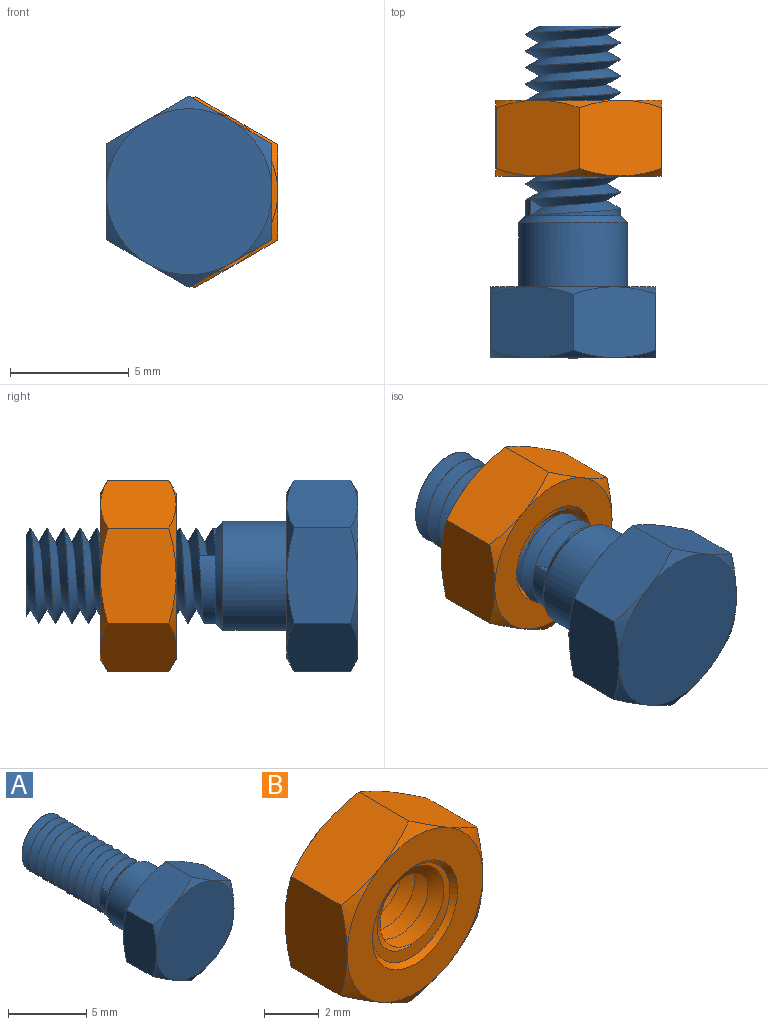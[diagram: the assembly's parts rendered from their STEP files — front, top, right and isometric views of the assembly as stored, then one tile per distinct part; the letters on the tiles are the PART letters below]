
ASSEMBLY  parts=2 mates=1
PART A: 27 faces, bbox 8.6x14.9x8.6 mm
  f0: cylinder r=2mm len=8mm, axis (0,-1,0), area 15.5mm2, adj f22,f23,f24,f25,f26
  f1: plane 7x7mm, normal (0,1,0), area 21.9mm2, adj f2,f3,f4,f5,f6,f7,f8
  f2: cylinder r=2.3mm len=4.6mm, axis (0,-1,0), area 39mm2, adj f1,f22
  f3: cone r=5.9mm half-angle=60deg, axis (0,-1,0), area 1.2mm2, adj f1,f9,f14
  f4: cone r=5.9mm half-angle=60deg, axis (0,-1,0), area 1.2mm2, adj f1,f9,f10
  f5: cone r=5.9mm half-angle=60deg, axis (0,-1,0), area 1.2mm2, adj f1,f10,f11
  f6: cone r=5.9mm half-angle=60deg, axis (0,-1,0), area 1.2mm2, adj f1,f11,f12
  f7: cone r=5.9mm half-angle=60deg, axis (0,-1,0), area 1.2mm2, adj f1,f12,f13
  f8: cone r=5.9mm half-angle=60deg, axis (0,-1,0), area 1.2mm2, adj f1,f13,f14
  f9: plane 3.83x3.34mm, normal (-0.5,0,0.87), area 11.3mm2, adj f3,f4,f10,f14,f15,f16
  f10: plane 3.83x3.34mm, normal (0.5,0,0.87), area 11.3mm2, adj f4,f5,f9,f11,f16,f17
  f11: plane 4.38x3.34mm, normal (1,0,0), area 11.3mm2, adj f5,f6,f10,f12,f17,f18
  f12: plane 3.83x3.34mm, normal (0.5,0,-0.87), area 11.3mm2, adj f6,f7,f11,f13,f18,f19
  f13: plane 3.83x3.34mm, normal (-0.5,0,-0.87), area 11.3mm2, adj f7,f8,f12,f14,f19,f20
  f14: plane 4.38x3.34mm, normal (-1,0,0), area 11.3mm2, adj f3,f8,f9,f13,f15,f20
  f15: cone r=5.9mm half-angle=60deg, axis (0,1,0), area 1.2mm2, adj f9,f14,f21
  f16: cone r=5.9mm half-angle=60deg, axis (0,1,0), area 1.2mm2, adj f9,f10,f21
  f17: cone r=5.9mm half-angle=60deg, axis (0,1,0), area 1.2mm2, adj f10,f11,f21
  f18: cone r=5.9mm half-angle=60deg, axis (0,1,0), area 1.2mm2, adj f11,f12,f21
  f19: cone r=5.9mm half-angle=60deg, axis (0,1,0), area 1.2mm2, adj f12,f13,f21
  f20: cone r=5.9mm half-angle=60deg, axis (0,1,0), area 1.2mm2, adj f13,f14,f21
  f21: plane 7x7mm, normal (0,-1,0), area 38.5mm2, adj f15,f16,f17,f18,f19,f20
  f22: cone r=2.3mm half-angle=45deg, axis (0,-1,0), area 5.7mm2, adj f0,f2,f24
  f23: plane 3.93x3.91mm, normal (0,1,0), area 9.3mm2, adj f0,f24,f25
  f24: bspline ~8.39x4.62mm, area 82.1mm2, adj f0,f22,f23,f25,f26
  f25: bspline ~8.16x4.62mm, area 78.6mm2, adj f0,f23,f24,f26
  f26: plane 0.69x0.54mm, normal (0.43,0,0.9), area 0.2mm2, adj f0,f24,f25
PART B: 27 faces, bbox 8.6x4.1x8.6 mm
  f0: bspline ~4.62x4mm, area 29.4mm2, adj f1,f2,f25,f26
  f1: bspline ~4.62x4mm, area 29.4mm2, adj f0,f2,f25,f26
  f2: cylinder r=2mm len=4mm, axis (0,1,0), area 1.2mm2, adj f0,f1,f23,f24
  f3: plane 7x7mm, normal (0,-1,0), area 23.3mm2, adj f7,f8,f10,f12,f14,f16,f23
  f4: plane 7x7mm, normal (0,1,0), area 23.3mm2, adj f5,f6,f9,f11,f13,f15,f24
  f5: cone r=6.04mm half-angle=60deg, axis (0,-1,0), area 1.2mm2, adj f4,f17,f22
  f6: cone r=6.04mm half-angle=60deg, axis (0,-1,0), area 1.2mm2, adj f4,f17,f18
  f7: cone r=6.04mm half-angle=60deg, axis (0,1,0), area 1.2mm2, adj f3,f17,f22
  f8: cone r=6.04mm half-angle=60deg, axis (0,1,0), area 1.2mm2, adj f3,f17,f18
  f9: cone r=6.04mm half-angle=60deg, axis (0,-1,0), area 1.2mm2, adj f4,f18,f19
  f10: cone r=6.04mm half-angle=60deg, axis (0,1,0), area 1.2mm2, adj f3,f18,f19
  f11: cone r=6.04mm half-angle=60deg, axis (0,-1,0), area 1.2mm2, adj f4,f19,f20
  f12: cone r=6.04mm half-angle=60deg, axis (0,1,0), area 1.2mm2, adj f3,f19,f20
  f13: cone r=6.04mm half-angle=60deg, axis (0,-1,0), area 1.2mm2, adj f4,f20,f21
  f14: cone r=6.04mm half-angle=60deg, axis (0,1,0), area 1.2mm2, adj f3,f20,f21
  f15: cone r=6.04mm half-angle=60deg, axis (0,-1,0), area 1.2mm2, adj f4,f21,f22
  f16: cone r=6.04mm half-angle=60deg, axis (0,1,0), area 1.2mm2, adj f3,f21,f22
  f17: plane 3.83x3.54mm, normal (0.5,0,0.87), area 12.1mm2, adj f5,f6,f7,f8,f18,f22
  f18: plane 4.38x3.54mm, normal (1,0,0), area 12.1mm2, adj f6,f8,f9,f10,f17,f19
  f19: plane 3.83x3.54mm, normal (0.5,0,-0.87), area 12.1mm2, adj f9,f10,f11,f12,f18,f20
  f20: plane 3.83x3.54mm, normal (-0.5,0,-0.87), area 12.1mm2, adj f11,f12,f13,f14,f19,f21
  f21: plane 4.38x3.54mm, normal (-1,0,0), area 12.1mm2, adj f13,f14,f15,f16,f20,f22
  f22: plane 3.83x3.54mm, normal (-0.5,0,0.87), area 12.1mm2, adj f5,f7,f15,f16,f17,f21
  f23: cone r=2mm half-angle=45deg, axis (0,-1,0), area 3.7mm2, adj f2,f3,f26
  f24: cone r=2.2mm half-angle=45deg, axis (0,1,0), area 3.7mm2, adj f2,f4,f25
  f25: plane 4.48x4.48mm, normal (0,1,0), area 3.3mm2, adj f0,f1,f24
  f26: plane 4.48x4.48mm, normal (0,-1,0), area 3.3mm2, adj f0,f1,f23
PLACE A t=(13.4,-14.63,4.06)mm fixed
PLACE B rot(axis=(0,1,0),60.2deg) t=(-2.36,-3.76,4.04)mm
MATE cylindrical A.f23 <-> B.f2  axis (0,1,0) through (-2.36,-0.63,4.04)mm
